# Revit family: Cumberland-Lloyd_Stools-
name_source: partatom
category: Furniture
revit_build: Autodesk Revit 2014 (Build: 20130308_1515(x64)
units: mm (PartAtom-declared; Revit-internal decimal feet)

## types (4) — shared parameters
Assembly Code = E2020200
Back = CUM - Linen - Beige
Depth = 21"
Glides = CUM - Black
Keynote = 12500
Leg = CUM - Stainless Steel
Low Emitting Finish = Yes
Low Emitting Material = Yes
Manufacturer = Cumberland
Salvage or Reuse = Yes
Seat = CUM - Linen - Beige
Type Comments = Lloyd
URL = www.cumberlandfurniture.com
Width = 18"
zero-valued in all types: Percentage of Recycled Content

## per-type parameters (varying)
| type | Bk | Description | Footrest Dist | Height | Model |
| 1063 - Counter | Yes | Counter, High Back | 6" | 21 1/2" | 1063 |
| 1064 - Bar Stool | No | Bar Stool, Backless | 9" | 26 1/2" | 1063 |
| 1065 - Bar Stool | Yes | Bar Stool, With Back | 9" | 26 1/2" | 1065 |
| 1062 - Counter | No | Counter, No Back | 6" | 21 1/2" | 1062 |

## geometry (parser evidence)
native form markers: Sweep x4
no freeform markers — native parametric forms only
